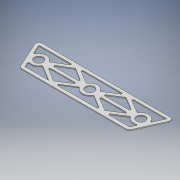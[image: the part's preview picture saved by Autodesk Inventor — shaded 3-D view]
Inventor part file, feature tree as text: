
AUTODESK INVENTOR PART (.ipt)
format: ipt  version: 2018.3 (Build 223284000, 284)  size: 233,984 bytes
history: native  units: mm
features: extrude x1, fillet x1, sketch x1
ambient origin geometry x8: Origin, YZ Plane, XZ Plane, XY Plane, X Axis, Y Axis, Z Axis, Center Point
bodies: Solid1 (feature_tree)
feature tree (3):
  extrude  "Extrusion1"  Depth=10.0mm
  fillet  "Fillet1"  Radius=10.0mm
  sketch  "Sketch1"  dims[d0=28.575mm d9=10.0mm d10=10.0mm d11=10.0mm d12=10.0mm d13=10.0mm d22=3.0mm d23=3.175mm d24=0.0mm d25=3.0mm]
